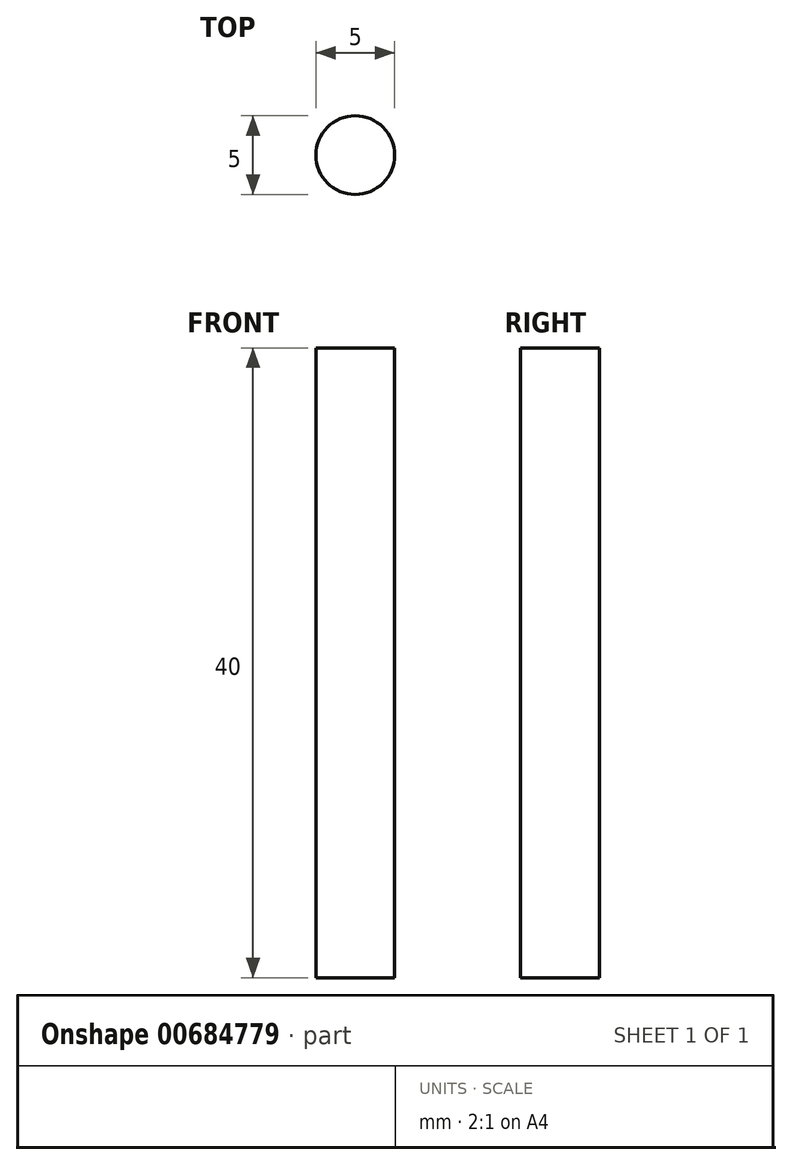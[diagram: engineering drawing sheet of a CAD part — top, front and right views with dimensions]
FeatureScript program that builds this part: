
annotation { "Feature Type Name" : "Feature", "Feature Type Description" : "" }
export const myFeature = defineFeature(function(context is Context, id is Id, definition is map)
    precondition{}
    {
        {
            var Q0;
            Q0=qCreatedBy(makeId("Top.planeOp"),FACE);
            var sketch = newSketch(context, id + "F0", { "sketchPlane" : qUnion([Q0])});
            skCircle(sketch, "E0", {"center": v(0, 0) * mm, "radius": 2.5 * mm});
            skSolve(sketch);
        }
        {
            var Q0;
            Q0 = qSketchRegion(id + "F0", true);
            extrude(context, id + "F1", {"entities" : qUnion([Q0]), "depth" : 40 * mm, "offsetDistance" : 25 * mm});
        }
    });
